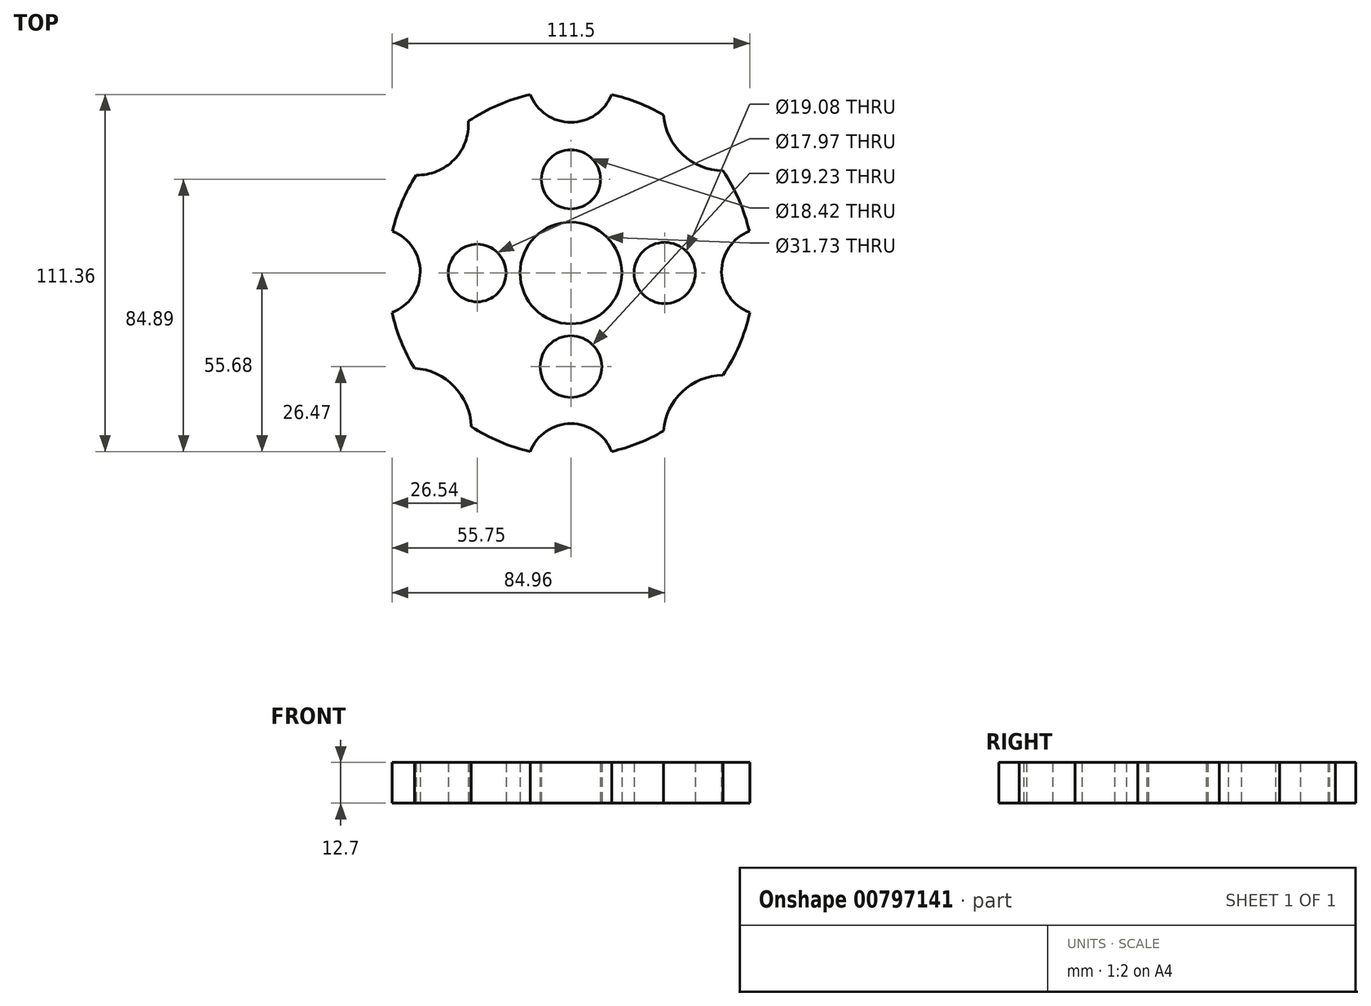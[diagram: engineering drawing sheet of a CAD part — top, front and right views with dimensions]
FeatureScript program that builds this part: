
annotation { "Feature Type Name" : "Feature", "Feature Type Description" : "" }
export const myFeature = defineFeature(function(context is Context, id is Id, definition is map)
    precondition{}
    {
        {
            var Q0;
            Q0=qCreatedBy(makeId("Top.planeOp"),FACE);
            var sketch = newSketch(context, id + "F0", { "sketchPlane" : qUnion([Q0])});
            skCircle(sketch, "E0", {"center": v(0, 0) * mm, "radius": 57.1 * mm});
            skArc(sketch, "E1", {"start": v(-55.75, -12.33) * mm, "mid": v(-46.99, 0.3) * mm, "end": v(-55.6, 13.03) * mm});
            skArc(sketch, "E2", {"start": v(12.68, -55.68) * mm, "mid": v(0, -47) * mm, "end": v(-12.68, -55.68) * mm});
            skArc(sketch, "E3", {"start": v(55.6, 13.05) * mm, "mid": v(57.1, 0.36) * mm, "end": v(55.75, -12.35) * mm});
            skArc(sketch, "E4", {"start": v(55.6, 13.05) * mm, "mid": v(46.94, 0.3) * mm, "end": v(55.75, -12.35) * mm});
            skArc(sketch, "E5", {"start": v(-12.68, 55.68) * mm, "mid": v(0, 47) * mm, "end": v(12.68, 55.68) * mm});
            skArc(sketch, "E6", {"start": v(47.35, -31.9) * mm, "mid": v(34.73, -37.01) * mm, "end": v(28.83, -49.29) * mm});
            skArc(sketch, "E7", {"start": v(28.88, 49.26) * mm, "mid": v(34.76, 36.98) * mm, "end": v(47.39, 31.86) * mm});
            skArc(sketch, "E8", {"start": v(-48.24, 30.56) * mm, "mid": v(-36.4, 35.36) * mm, "end": v(-31.94, 47.33) * mm});
            skCircle(sketch, "E9", {"center": v(0, 29.21) * mm, "radius": 9.21 * mm});
            skCircle(sketch, "E10", {"center": v(0, -29.21) * mm, "radius": 9.62 * mm});
            skCircle(sketch, "E11", {"center": v(-29.21, 0) * mm, "radius": 8.99 * mm});
            skCircle(sketch, "E12", {"center": v(29.21, 0) * mm, "radius": 9.54 * mm});
            skCircle(sketch, "E13", {"center": v(0, 0) * mm, "radius": 15.86 * mm});
            skArc(sketch, "E14", {"start": v(-31.07, -47.91) * mm, "mid": v(-36.4, -35.38) * mm, "end": v(-48.77, -29.7) * mm});
            skSolve(sketch);
        }
        {
            var Q0;
            {var subQ3=sQuery(id+"F0.wireOp",EDGE,"E1");Q0=makeQuery(id+"F0.imprint","IMPRINT",FACE,{"disambiguationData":[TD([[makeQuery(id+"F0.imprint","IMPRINT",EDGE,{"derivedFrom":subQ3}),-1.0]])]});}
            extrude(context, id + "F1", {"entities" : qUnion([Q0]), "endBound" : BoundingType.SYMMETRIC, "depth" : 12.7 * mm, "offsetDistance" : 25.4 * mm});
        }
    });
